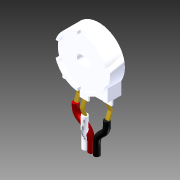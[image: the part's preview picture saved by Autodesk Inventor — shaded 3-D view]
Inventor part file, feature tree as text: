
AUTODESK INVENTOR PART (.ipt)
format: ipt  version: 2012 (Build 160160000, 160)  size: 371,200 bytes
history: native  units: in
note: dims shown in document units (in); Inventor stores cm internally (conversion verified against a paired STEP export)
features: other x1, imported_body x1, plane x1, split x1
ambient origin geometry x8: Origin, YZ Plane, XZ Plane, XY Plane, X Axis, Y Axis, Z Axis, Center Point
feature tree (4):
  parser-record x1  (decoder bookkeeping rows leaked as tree rows — omitted from the tree; the rows remain in map.json)
  imported_body  "Base1"
  plane  "Work Plane1"
  split  "Split1"
